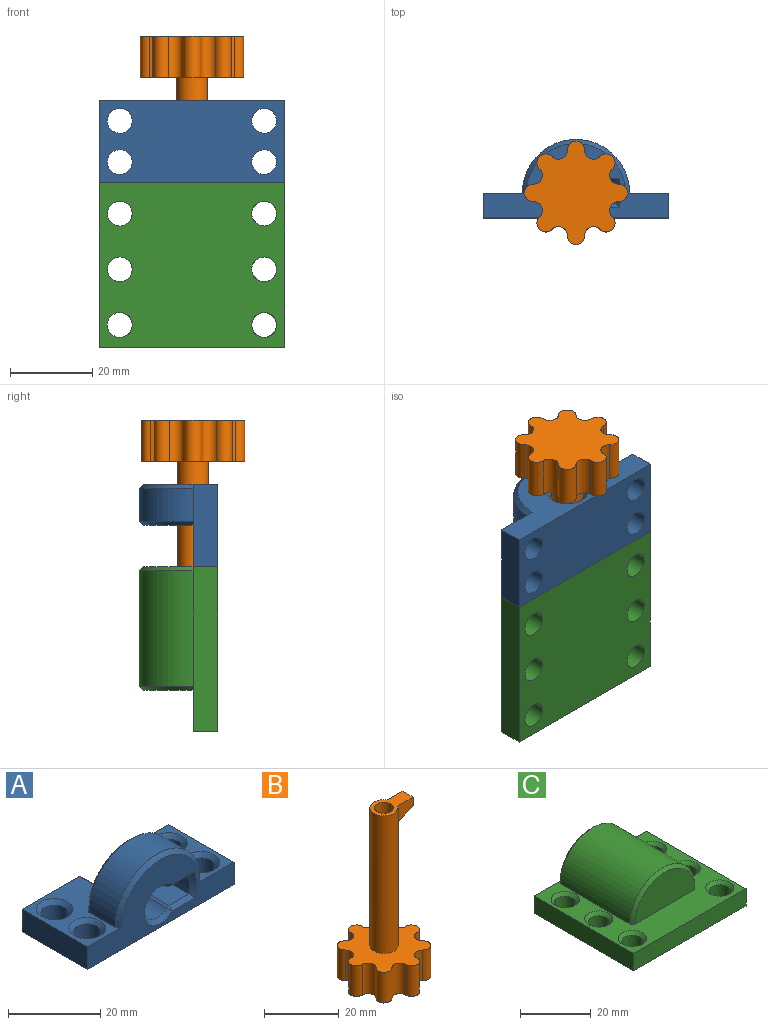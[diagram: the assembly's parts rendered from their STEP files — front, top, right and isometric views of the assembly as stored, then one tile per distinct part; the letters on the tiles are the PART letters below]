
ASSEMBLY  parts=3 mates=7
PART A: 41 faces, bbox 45.1x20.1x19.1 mm
  f0: cone r=3mm half-angle=45deg, axis (0,0,1), area 31.1mm2, adj f1,f8
  f1: cylinder r=3mm len=6mm, axis (0,0,1), area 94.2mm2, adj f0,f6
  f2: cone r=3mm half-angle=45deg, axis (0,0,1), area 31.1mm2, adj f3,f8
  f3: cylinder r=3mm len=6mm, axis (0,0,1), area 94.2mm2, adj f2,f6
  f4: cone r=3mm half-angle=45deg, axis (0,0,1), area 31.1mm2, adj f5,f10
  f5: cylinder r=3mm len=6mm, axis (0,0,1), area 94.2mm2, adj f4,f6
  f6: plane 45x20mm, normal (0,0,-1), area 786.9mm2, adj f1,f3,f5,f7,f15,f16,f18,f19
  f7: plane 20x6mm, normal (1,0,0), area 120mm2, adj f6,f8,f16,f18
  f8: plane 20x11.55mm, normal (0,0,1), area 110.9mm2, adj f0,f2,f7,f9,f16,f17,f18,f21
  f9: cylinder r=13mm len=26mm, axis (0,1,0), area 326.7mm2, adj f8,f10,f21,f22
  f10: plane 20x17.6mm, normal (0,0,1), area 171.5mm2, adj f4,f9,f15,f16,f17,f18,f20,f21
  f11: cylinder r=4mm len=18mm, axis (0,1,0), area 238mm2, adj f25,f28,f31,f32,f35,f36
  f12: plane 8x6.11mm, normal (0,0,-1), area 48.9mm2, adj f13,f30,f35,f40
  f13: cylinder r=10mm len=18mm, axis (0,1,0), area 56.6mm2, adj f12,f14,f23,f24,f27,f39
  f14: plane 18x6.11mm, normal (0,0,1), area 110mm2, adj f13,f26,f32,f37
  f15: plane 20x6mm, normal (-1,0,0), area 120mm2, adj f6,f10,f16,f18
  f16: plane 45x18mm, normal (0,-1,0), area 373.9mm2, adj f6,f7,f8,f10,f15,f22,f36,f37
  f17: plane 24x12mm, normal (0,1,0), area 165mm2, adj f8,f10,f21,f27,f30,f31
  f18: plane 45x6mm, normal (0,1,0), area 208.8mm2, adj f6,f7,f8,f10,f15,f23,f25,f26
  f19: cylinder r=3mm len=6mm, axis (0,0,1), area 94.2mm2, adj f6,f20
  f20: cone r=3mm half-angle=45deg, axis (0,0,1), area 31.1mm2, adj f10,f19
  f21: cone r=12mm half-angle=45deg, axis (0,-1,0), area 55.5mm2, adj f8,f9,f10,f17
  f22: cone r=13mm half-angle=45deg, axis (0,1,0), area 55.5mm2, adj f8,f9,f10,f16
  f23: cone r=11mm half-angle=45deg, axis (0,1,0), area 3.7mm2, adj f8,f13,f18,f24,f26
  f24: plane 11.01x1.05mm, normal (-0.67,0,0.74), area 13.5mm2, adj f8,f13,f23,f27
  f25: cone r=5mm half-angle=45deg, axis (0,1,0), area 14.6mm2, adj f10,f11,f18,f28,f29
  f26: plane 6.89x1.03mm, normal (0,0.71,0.71), area 9.2mm2, adj f14,f18,f23,f29
  f27: cone r=11mm half-angle=45deg, axis (0,1,0), area 4.9mm2, adj f8,f13,f17,f24,f30
  f28: plane 10.9x0.98mm, normal (0.63,0,0.77), area 12.6mm2, adj f10,f11,f25,f31
  f29: plane 1x1mm, normal (-0.28,0.68,0.68), area 0.5mm2, adj f25,f26,f32
  f30: plane 6.89x1.03mm, normal (0,0.71,-0.71), area 9.2mm2, adj f12,f17,f27,f33
  f31: cone r=5mm half-angle=45deg, axis (0,1,0), area 15.6mm2, adj f10,f11,f17,f28,f33
  f32: plane 18x0.71mm, normal (-0.39,0,0.92), area 13.9mm2, adj f11,f14,f29,f34
  f33: plane 1x1mm, normal (-0.28,0.68,-0.68), area 0.5mm2, adj f30,f31,f35
  f34: plane 1x1mm, normal (-0.28,-0.68,0.68), area 0.5mm2, adj f32,f36,f37
  f35: plane 8x0.71mm, normal (-0.39,0,-0.92), area 6.2mm2, adj f11,f12,f33,f38
  f36: cone r=4mm half-angle=45deg, axis (0,-1,0), area 30.1mm2, adj f11,f16,f34,f38
  f37: plane 6.89x1.03mm, normal (0,-0.71,0.71), area 9.2mm2, adj f14,f16,f34,f39
  f38: plane 1x1mm, normal (-0.28,-0.68,-0.68), area 0.5mm2, adj f35,f36,f40
  f39: cone r=10mm half-angle=45deg, axis (0,-1,0), area 8.6mm2, adj f13,f16,f37,f40
  f40: plane 6.89x1.03mm, normal (0,-0.71,-0.71), area 9.2mm2, adj f12,f16,f38,f39
PART B: 26 faces, bbox 25x25x55 mm
  f0: cylinder r=2.13mm len=10mm, axis (0,0,-1), area 67.8mm2, adj f1,f15,f16,f17
  f1: cylinder r=2.13mm len=10mm, axis (0,0,-1), area 51.1mm2, adj f0,f2,f16,f17
  f2: cylinder r=2.13mm len=10mm, axis (0,0,-1), area 67.8mm2, adj f1,f3,f16,f17
  f3: cylinder r=2.13mm len=10mm, axis (0,0,-1), area 51.1mm2, adj f2,f4,f16,f17
  f4: cylinder r=2.13mm len=10mm, axis (0,0,-1), area 67.8mm2, adj f3,f5,f16,f17
  f5: cylinder r=2.13mm len=10mm, axis (0,0,-1), area 51.1mm2, adj f4,f6,f16,f17
  f6: cylinder r=2.13mm len=10mm, axis (0,0,-1), area 67.8mm2, adj f5,f7,f16,f17
  f7: cylinder r=2.13mm len=10mm, axis (0,0,-1), area 51.1mm2, adj f6,f8,f16,f17
  f8: cylinder r=2.13mm len=10mm, axis (0,0,-1), area 67.8mm2, adj f7,f9,f16,f17
  f9: cylinder r=2.13mm len=10mm, axis (0,0,-1), area 51.1mm2, adj f8,f10,f16,f17
  f10: cylinder r=2.13mm len=10mm, axis (0,0,-1), area 67.8mm2, adj f9,f11,f16,f17
  f11: cylinder r=2.13mm len=10mm, axis (0,0,-1), area 51.1mm2, adj f10,f12,f16,f17
  f12: cylinder r=2.13mm len=10mm, axis (0,0,-1), area 67.8mm2, adj f11,f13,f16,f17
  f13: cylinder r=2.13mm len=10mm, axis (0,0,-1), area 51.1mm2, adj f12,f14,f16,f17
  f14: cylinder r=2.13mm len=10mm, axis (0,0,-1), area 67.8mm2, adj f13,f15,f16,f17
  f15: cylinder r=2.13mm len=10mm, axis (0,0,-1), area 51.1mm2, adj f0,f14,f16,f17
  f16: plane 25x25mm, normal (0,0,1), area 323.4mm2, adj f0,f1,f2,f3,f4,f5,f6,f7
  f17: plane 25x25mm, normal (0,0,-1), area 367.6mm2, adj f0,f1,f2,f3,f4,f5,f6,f7
  f18: cylinder r=3.75mm len=45mm, axis (0,0,-1), area 1037.7mm2, adj f16,f19,f20,f21,f22
  f19: plane 12.75x7.5mm, normal (0,0,1), area 46.3mm2, adj f18,f20,f21,f23,f24
  f20: plane 5.83x5.52mm, normal (0,-1,0), area 24.3mm2, adj f18,f19,f22,f23
  f21: plane 5.83x5.52mm, normal (0,1,0), area 24.3mm2, adj f18,f19,f22,f23
  f22: plane 5.83x4mm, normal (0.42,0,-0.91), area 24mm2, adj f18,f20,f21,f23
  f23: plane 4x2.8mm, normal (1,0,0), area 11.2mm2, adj f19,f20,f21,f22
  f24: cylinder r=2.5mm len=10mm, axis (0,0,1), area 157.1mm2, adj f19,f25
  f25: plane 5x5mm, normal (0,0,1), area 19.6mm2, adj f24
PART C: 42 faces, bbox 45.1x40.1x19.1 mm
  f0: cone r=3mm half-angle=45deg, axis (0,0,1), area 31.1mm2, adj f1,f17
  f1: cylinder r=3mm len=6mm, axis (0,0,1), area 94.2mm2, adj f0,f14
  f2: cone r=3mm half-angle=45deg, axis (0,0,1), area 31.1mm2, adj f3,f17
  f3: cylinder r=3mm len=6mm, axis (0,0,1), area 94.2mm2, adj f2,f14
  f4: cone r=3mm half-angle=45deg, axis (0,0,1), area 31.1mm2, adj f5,f17
  f5: cylinder r=3mm len=6mm, axis (0,0,1), area 94.2mm2, adj f4,f14
  f6: cone r=3mm half-angle=45deg, axis (0,0,1), area 31.1mm2, adj f7,f17
  f7: cylinder r=3mm len=6mm, axis (0,0,1), area 94.2mm2, adj f6,f14
  f8: cone r=3mm half-angle=45deg, axis (0,0,1), area 31.1mm2, adj f9,f17
  f9: cylinder r=3mm len=6mm, axis (0,0,1), area 94.2mm2, adj f8,f14
  f10: cylinder r=4mm len=24.5mm, axis (0,-1,0), area 317.2mm2, adj f11,f21,f26,f29,f33,f35,f37,f38
  f11: plane 19.03x7.42mm, normal (0,-1,0), area 93.6mm2, adj f10,f20,f26,f35
  f12: plane 45x18mm, normal (0,1,0), area 373.9mm2, adj f14,f15,f17,f18,f30,f32,f33,f34
  f13: plane 24x12mm, normal (0,-1,0), area 226.2mm2, adj f17,f40
  f14: plane 45x40mm, normal (0,0,-1), area 1630.4mm2, adj f1,f3,f5,f7,f9,f12,f15,f18
  f15: plane 40x6mm, normal (1,0,0), area 240mm2, adj f12,f14,f17,f19
  f16: cylinder r=13mm len=28mm, axis (0,1,0), area 1143.5mm2, adj f17,f40,f41
  f17: plane 45x40mm, normal (0,0,1), area 720.4mm2, adj f0,f2,f4,f6,f8,f12,f13,f15
  f18: plane 40x6mm, normal (-1,0,0), area 240mm2, adj f12,f14,f17,f19
  f19: plane 45x6mm, normal (0,-1,0), area 270mm2, adj f14,f15,f17,f18
  f20: cylinder r=10mm len=24.5mm, axis (0,-1,0), area 407.8mm2, adj f11,f21,f22,f23,f24,f25,f26,f32
  f21: plane 20x14mm, normal (0,1,0), area 219.5mm2, adj f10,f20,f23,f25,f29,f39
  f22: plane 15.5x6.11mm, normal (0,0,-1), area 94.7mm2, adj f20,f34,f35,f37
  f23: plane 24.5x6.11mm, normal (0,0,1), area 149.7mm2, adj f20,f21,f29,f30
  f24: plane 6.35x6mm, normal (0,-1,0), area 31.1mm2, adj f20,f25,f26,f38
  f25: plane 12.86x7.06mm, normal (0,0,1), area 85.3mm2, adj f20,f21,f24,f38,f39
  f26: plane 6.6x5mm, normal (0,0,-1), area 27mm2, adj f10,f11,f20,f24,f38
  f27: cylinder r=3mm len=6mm, axis (0,0,1), area 94.2mm2, adj f14,f28
  f28: cone r=3mm half-angle=45deg, axis (0,0,1), area 31.1mm2, adj f17,f27
  f29: plane 24.5x0.71mm, normal (0.39,0,0.92), area 19mm2, adj f10,f21,f23,f31
  f30: plane 6.89x1.03mm, normal (0,0.71,0.71), area 9.2mm2, adj f12,f23,f31,f32
  f31: plane 1x1mm, normal (0.28,0.68,0.68), area 0.5mm2, adj f29,f30,f33
  f32: cone r=10mm half-angle=45deg, axis (0,1,0), area 8.6mm2, adj f12,f20,f30,f34
  f33: cone r=5mm half-angle=45deg, axis (0,1,0), area 30.1mm2, adj f10,f12,f31,f36
  f34: plane 6.89x1.03mm, normal (0,0.71,-0.71), area 9.2mm2, adj f12,f22,f32,f36
  f35: plane 7.81x1.07mm, normal (0,-0.71,-0.71), area 9.7mm2, adj f10,f11,f20,f22,f37
  f36: plane 1x1mm, normal (0.28,0.68,-0.68), area 0.5mm2, adj f33,f34,f37
  f37: plane 15.8x0.71mm, normal (0.39,0,-0.92), area 12.1mm2, adj f10,f22,f35,f36
  f38: cone r=4mm half-angle=45deg, axis (0,-1,0), area 9.4mm2, adj f10,f24,f25,f26,f39
  f39: plane 13.02x0.49mm, normal (-0.24,0,0.97), area 6.2mm2, adj f10,f21,f25,f38
  f40: cone r=13mm half-angle=45deg, axis (0,1,0), area 55.5mm2, adj f13,f16,f17
  f41: cone r=12mm half-angle=45deg, axis (0,-1,0), area 55.5mm2, adj f12,f16,f17
PLACE A rot(axis=(-1,0,0),90deg) t=(0,0,29.9)mm
PLACE B rot(axis=(0,1,0),180deg) t=(0,6,55.4)mm
PLACE C rot(axis=(0,0.71,0.71),180deg) t=(0,0,19.9)mm
MATE planar A.f6 <-> C.f14  axis (0,-1,0) through (0,0,29.9)mm
MATE parallel B.f18 <-> A.f16  axis (0,0,-1) through (0,6,45.4)mm
MATE planar A.f15 <-> C.f15  axis (-1,0,0) through (-22.5,3,29.9)mm
MATE planar C.f12 <-> A.f18  axis (0,0,1) through (-17.25,6,19.9)mm
MATE cylindrical B.f18 <-> A.f11  axis (0,0,1) through (0,6,22.9)mm
MATE planar B.f19 <-> C.f10  axis (0,0,-1) through (-6.09,8,0.4)mm
MATE parallel B.f21 <-> C.f25  axis (0,1,0) through (-5.77,8,2.55)mm
